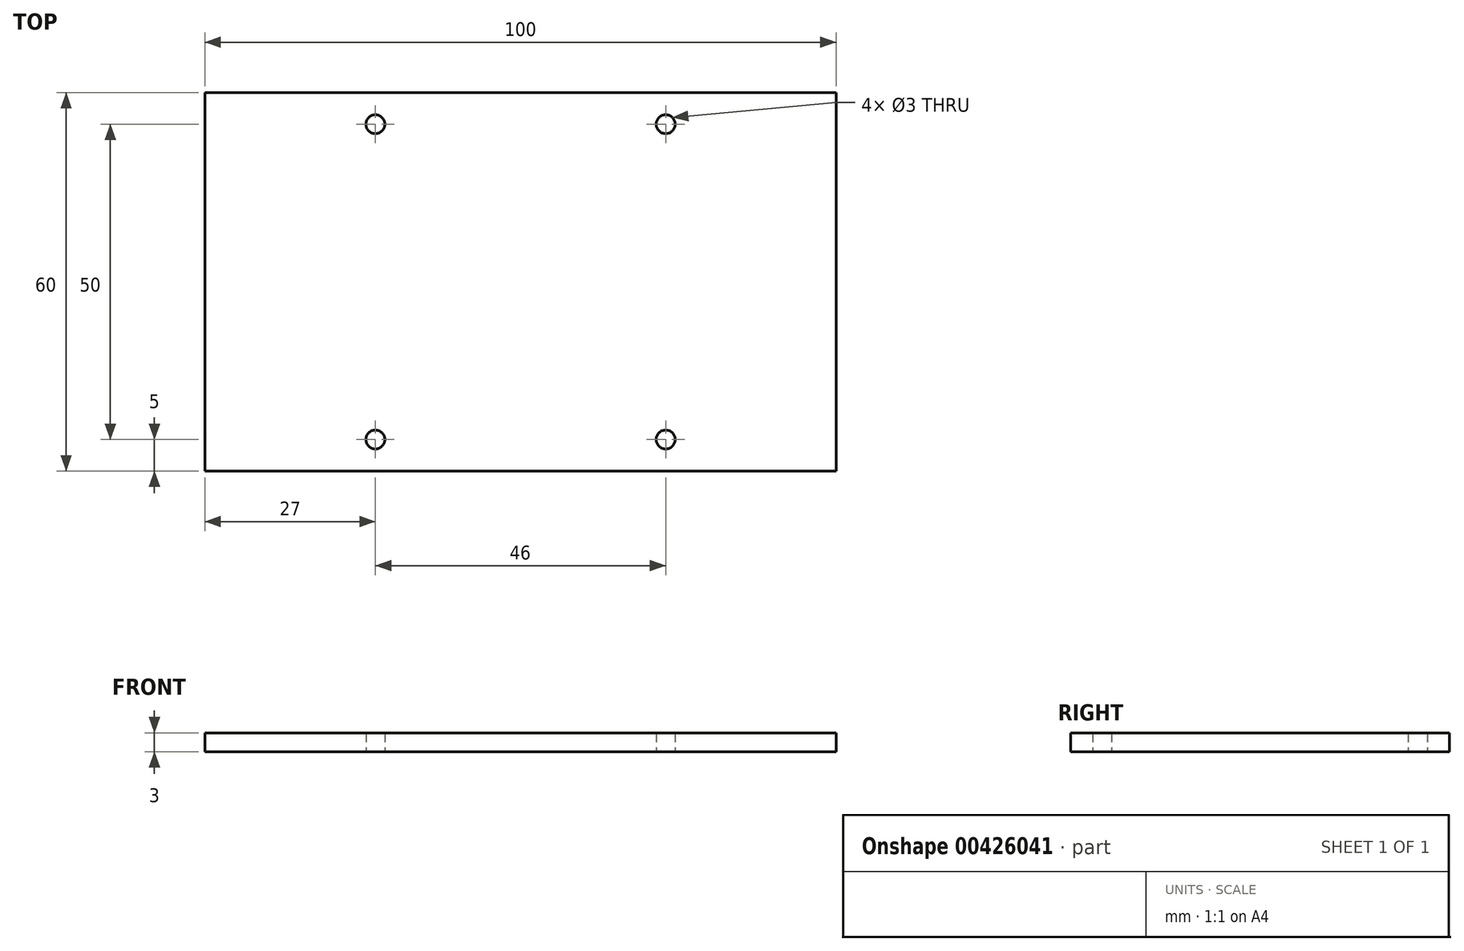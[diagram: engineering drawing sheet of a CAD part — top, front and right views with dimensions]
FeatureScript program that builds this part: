
annotation { "Feature Type Name" : "Feature", "Feature Type Description" : "" }
export const myFeature = defineFeature(function(context is Context, id is Id, definition is map)
    precondition{}
    {
        {
            var Q0;
            Q0=qCreatedBy(makeId("Top.planeOp"),FACE);
            var sketch = newSketch(context, id + "F0", { "sketchPlane" : qUnion([Q0])});
            skLineSegment(sketch, "E0.bottom", {"start": v(50, -30) * mm, "end": v(-50, -30) * mm});
            skLineSegment(sketch, "E0.top", {"start": v(50, 30) * mm, "end": v(-50, 30) * mm});
            skLineSegment(sketch, "E0.left", {"start": v(50, -30) * mm, "end": v(50, 30) * mm});
            skLineSegment(sketch, "E0.right", {"start": v(-50, -30) * mm, "end": v(-50, 30) * mm});
            skPoint(sketch, "E0.middle", {"position": v(0, 0) * mm});
            skCircle(sketch, "E1", {"center": v(-23, 25) * mm, "radius": 1.5 * mm});
            skCircle(sketch, "E2.MirrorC", {"center": v(23, 25) * mm, "radius": 1.5 * mm});
            skCircle(sketch, "E3.MirrorC", {"center": v(-23, -25) * mm, "radius": 1.5 * mm});
            skCircle(sketch, "E4.MirrorC", {"center": v(23, -25) * mm, "radius": 1.5 * mm});
            skSolve(sketch);
        }
        {
            var Q0;
            Q0=makeQuery(id+"F0.imprint","IMPRINT",FACE,{"disambiguationData":[TD([[makeQuery(id+"F0.imprint","IMPRINT",EDGE,{"derivedFrom":sQuery(id+"F0.wireOp",EDGE,"E0.bottom")}),-1.0]])]});
            extrude(context, id + "F1", {"entities" : qUnion([Q0]), "depth" : 3 * mm});
        }
    });
